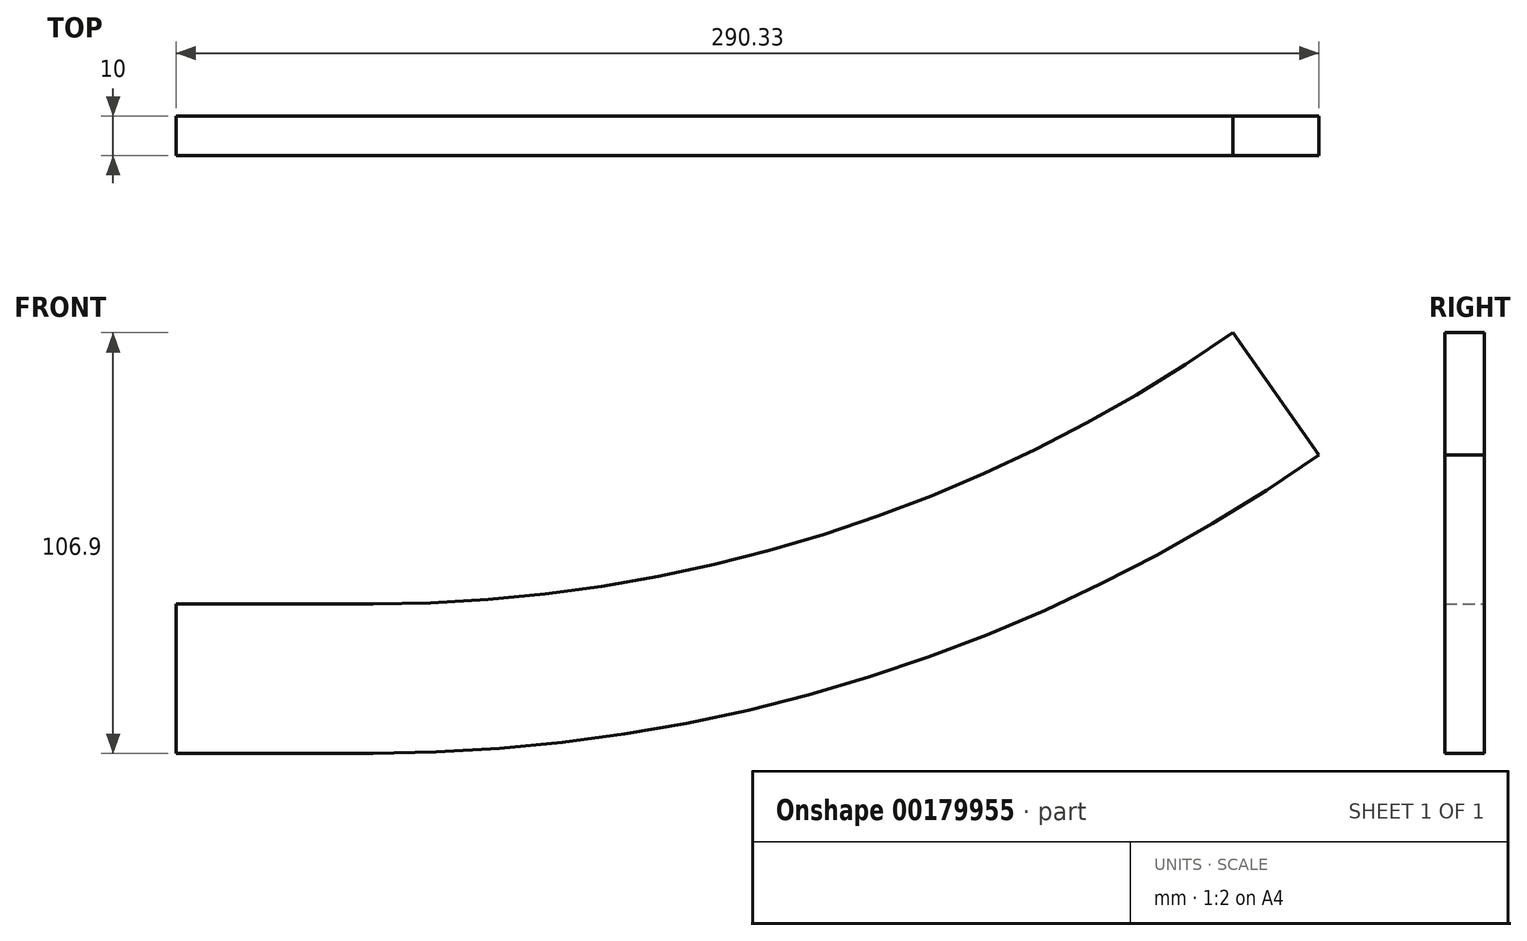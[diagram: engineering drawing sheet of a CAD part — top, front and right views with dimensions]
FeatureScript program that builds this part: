
annotation { "Feature Type Name" : "Feature", "Feature Type Description" : "" }
export const myFeature = defineFeature(function(context is Context, id is Id, definition is map)
    precondition{}
    {
        {
            var Q0;
            Q0=qCreatedBy(makeId("Front.planeOp"),FACE);
            var sketch = newSketch(context, id + "F0", { "sketchPlane" : qUnion([Q0])});
            skLineSegment(sketch, "E0.left", {"start": v(0, 0) * mm, "end": v(0, 400) * mm, "construction": true});
            skArc(sketch, "E1", {"start": v(0, 0) * mm, "mid": v(200, 53.59) * mm, "end": v(346.41, 200) * mm, "construction": true});
            skLineSegment(sketch, "E2", {"start": v(0, 400) * mm, "end": v(346.41, 200) * mm, "construction": true});
            skArc(sketch, "E3.0", {"start": v(0, -19) * mm, "mid": v(209.5, 37.14) * mm, "end": v(362.86, 190.5) * mm});
            skArc(sketch, "E4.0", {"start": v(0, 19) * mm, "mid": v(190.5, 70.04) * mm, "end": v(329.96, 209.5) * mm});
            skLineSegment(sketch, "E5", {"start": v(0, 400) * mm, "end": v(240.33, 56.78) * mm});
            skLineSegment(sketch, "E6", {"start": v(0, -19) * mm, "end": v(0, 19) * mm});
            skLineSegment(sketch, "E7", {"start": v(0, 19) * mm, "end": v(-50, 19) * mm});
            skLineSegment(sketch, "E8", {"start": v(-50, 19) * mm, "end": v(-50, -19) * mm});
            skLineSegment(sketch, "E9", {"start": v(-50, -19) * mm, "end": v(0, -19) * mm});
            skSolve(sketch);
        }
        {
            var Q0;
            Q0=qSketchRegion(id+"F0",true);
            extrude(context, id + "F1", {"entities" : qUnion([Q0]), "depth" : 10 * mm});
        }
    });
